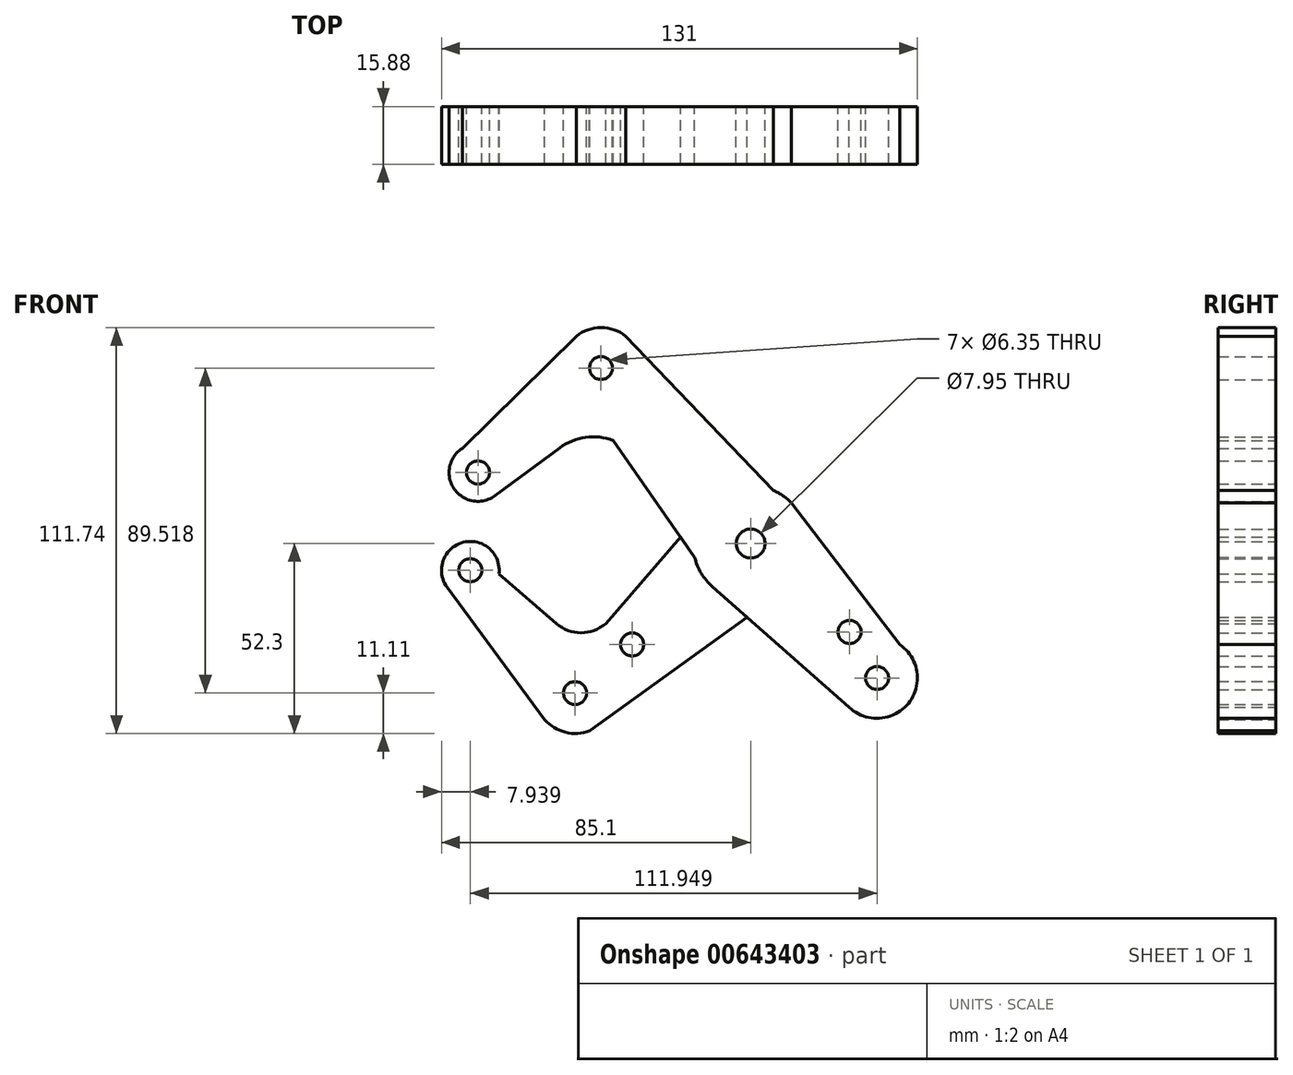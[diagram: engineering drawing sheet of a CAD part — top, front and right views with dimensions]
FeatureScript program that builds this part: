
annotation { "Feature Type Name" : "Feature", "Feature Type Description" : "" }
export const myFeature = defineFeature(function(context is Context, id is Id, definition is map)
    precondition{}
    {
        {
            var Q0;
            Q0=qCreatedBy(makeId("Front.planeOp"),FACE);
            var sketch = newSketch(context, id + "F0", { "sketchPlane" : qUnion([Q0])});
            skCircle(sketch, "E0", {"center": v(0, 0) * mm, "radius": 3.98 * mm});
            skCircle(sketch, "E1", {"center": v(0, 0) * mm, "radius": 15.88 * mm});
            skCircle(sketch, "E2", {"center": v(-41.19, 48.33) * mm, "radius": 11.11 * mm});
            skCircle(sketch, "E3", {"center": v(-41.19, 48.33) * mm, "radius": 3.18 * mm});
            skCircle(sketch, "E4", {"center": v(-75.06, 19.55) * mm, "radius": 3.18 * mm});
            skCircle(sketch, "E5", {"center": v(-75.06, 19.55) * mm, "radius": 7.94 * mm});
            skCircle(sketch, "E6", {"center": v(0, 0) * mm, "radius": 3.18 * mm});
            skCircle(sketch, "E7", {"center": v(34.79, -37.02) * mm, "radius": 3.18 * mm});
            skCircle(sketch, "E8", {"center": v(34.79, -37.02) * mm, "radius": 11.11 * mm});
            skLineSegment(sketch, "E9", {"start": v(-41.19, 48.33) * mm, "end": v(-75.06, 19.55) * mm, "construction": true});
            skLineSegment(sketch, "E10", {"start": v(-41.19, 48.33) * mm, "end": v(0, 0) * mm, "construction": true});
            skLineSegment(sketch, "E11", {"start": v(0, 0) * mm, "end": v(34.79, -37.02) * mm, "construction": true});
            skCircle(sketch, "E12", {"center": v(27.23, -24.34) * mm, "radius": 3.18 * mm});
            skLineSegment(sketch, "E13", {"start": v(0, 0) * mm, "end": v(-48.33, -41.19) * mm, "construction": true});
            skCircle(sketch, "E14", {"center": v(-48.33, -41.19) * mm, "radius": 11.11 * mm});
            skCircle(sketch, "E15", {"center": v(-48.33, -41.19) * mm, "radius": 3.18 * mm});
            skCircle(sketch, "E16", {"center": v(-32.61, -27.8) * mm, "radius": 3.18 * mm});
            skLineSegment(sketch, "E17", {"start": v(-48.33, -41.19) * mm, "end": v(-77.16, -7.36) * mm, "construction": true});
            skCircle(sketch, "E18", {"center": v(-77.16, -7.36) * mm, "radius": 3.18 * mm});
            skCircle(sketch, "E19", {"center": v(-77.16, -7.36) * mm, "radius": 7.94 * mm});
            skLineSegment(sketch, "E20", {"start": v(-79.35, 26.23) * mm, "end": v(-48.03, 57.09) * mm});
            skLineSegment(sketch, "E21", {"start": v(11.26, 11.2) * mm, "end": v(41.01, -27.81) * mm});
            skLineSegment(sketch, "E22", {"start": v(27.1, -45.04) * mm, "end": v(-12.2, -10.4) * mm});
            skLineSegment(sketch, "E23", {"start": v(-56.75, -48.44) * mm, "end": v(-83.55, -12.07) * mm});
            skLineSegment(sketch, "E24", {"start": v(-69.3, -8.4) * mm, "end": v(-53.49, -22.06) * mm});
            skArc(sketch, "E25", {"start": v(-53.49, -22.06) * mm, "mid": v(-46.7, -24.58) * mm, "end": v(-39.9, -22.06) * mm});
            skLineSegment(sketch, "E26", {"start": v(-39.9, -22.06) * mm, "end": v(-13.01, 9.1) * mm});
            skLineSegment(sketch, "E27", {"start": v(-44.26, -51.53) * mm, "end": v(10.96, -11.67) * mm});
            skLineSegment(sketch, "E28", {"start": v(-34.35, 57.09) * mm, "end": v(6.26, 14.59) * mm});
            skLineSegment(sketch, "E29", {"start": v(-70.34, 13.17) * mm, "end": v(-52.54, 26.34) * mm});
            skArc(sketch, "E30", {"start": v(-52.54, 26.34) * mm, "mid": v(-45.43, 29.24) * mm, "end": v(-37.8, 28.38) * mm});
            skLineSegment(sketch, "E31", {"start": v(-37.8, 28.38) * mm, "end": v(-15.43, -3.75) * mm});
            skSolve(sketch);
        }
        {
            var Q0;
            Q0=makeQuery(id+"F0.imprint","IMPRINT",FACE,{"disambiguationData":[TD([[makeQuery(id+"F0.imprint","IMPRINT",EDGE,{"derivedFrom":sQuery(id+"F0.wireOp",EDGE,"E16")}),-1.0]])]});
            var Q1;
            Q1=makeQuery(id+"F0.imprint","IMPRINT",FACE,{"disambiguationData":[TD([[makeQuery(id+"F0.imprint","IMPRINT",EDGE,{"derivedFrom":sQuery(id+"F0.wireOp",EDGE,"E18")}),-1.0]])]});
            var Q2;
            Q2=makeQuery(id+"F0.imprint","IMPRINT",FACE,{"disambiguationData":[TD([[makeQuery(id+"F0.imprint","IMPRINT",EDGE,{"derivedFrom":sQuery(id+"F0.wireOp",EDGE,"E15")}),-1.0]])]});
            extrude(context, id + "F1", {"entities" : qUnion([Q0, Q1, Q2]), "depth" : 15.88 * mm, "offsetDistance" : 25.4 * mm});
        }
        {
            var Q0;
            {var subQ0=sQuery(id+"F0.wireOp",EDGE,"E26");var subQ1=sQuery(id+"F0.wireOp",EDGE,"E1");var subQ2=makeQuery(id+"F0.imprint","INTERSECT",VERTEX,{"derivedFrom":[subQ1,subQ0]});Q0=makeQuery(id+"F0.imprint","IMPRINT",FACE,{"disambiguationData":[TD([[makeQuery(id+"F0.imprint","IMPRINT",EDGE,{"disambiguationData":[TD([[subQ2,-1.0]])],"derivedFrom":subQ1}),-1.0]])]});}
            var Q1;
            Q1=makeQuery(id+"F0.imprint","IMPRINT",FACE,{"disambiguationData":[TD([[makeQuery(id+"F0.imprint","IMPRINT",EDGE,{"derivedFrom":sQuery(id+"F0.wireOp",EDGE,"E0")}),-1.0]])]});
            var Q2;
            Q2=makeQuery(id+"F0.imprint","IMPRINT",FACE,{"disambiguationData":[TD([[makeQuery(id+"F0.imprint","IMPRINT",EDGE,{"derivedFrom":sQuery(id+"F0.wireOp",EDGE,"E12")}),-1.0]])]});
            var Q3;
            {var subQ0=sQuery(id+"F0.wireOp",EDGE,"E22");var subQ1=sQuery(id+"F0.wireOp",EDGE,"E1");var subQ2=makeQuery(id+"F0.imprint","INTERSECT",VERTEX,{"derivedFrom":[subQ1,subQ0]});Q3=makeQuery(id+"F0.imprint","IMPRINT",FACE,{"disambiguationData":[TD([[makeQuery(id+"F0.imprint","IMPRINT",EDGE,{"disambiguationData":[TD([[subQ2,-1.0]])],"derivedFrom":subQ1}),-1.0]])]});}
            var Q4;
            {var subQ10=sQuery(id+"F0.wireOp",EDGE,"E29");Q4=makeQuery(id+"F0.imprint","IMPRINT",FACE,{"disambiguationData":[TD([[makeQuery(id+"F0.imprint","IMPRINT",EDGE,{"derivedFrom":subQ10}),1.0]])]});}
            var Q5;
            Q5=makeQuery(id+"F0.imprint","IMPRINT",FACE,{"disambiguationData":[TD([[makeQuery(id+"F0.imprint","IMPRINT",EDGE,{"derivedFrom":sQuery(id+"F0.wireOp",EDGE,"E3")}),-1.0]])]});
            var Q6;
            Q6=makeQuery(id+"F0.imprint","IMPRINT",FACE,{"disambiguationData":[TD([[makeQuery(id+"F0.imprint","IMPRINT",EDGE,{"derivedFrom":sQuery(id+"F0.wireOp",EDGE,"E4")}),-1.0]])]});
            var Q7;
            Q7=makeQuery(id+"F0.imprint","IMPRINT",FACE,{"disambiguationData":[TD([[makeQuery(id+"F0.imprint","IMPRINT",EDGE,{"derivedFrom":sQuery(id+"F0.wireOp",EDGE,"E7")}),-1.0]])]});
            extrude(context, id + "F2", {"entities" : qUnion([Q0, Q1, Q2, Q3, Q4, Q5, Q6, Q7]), "depth" : 15.88 * mm, "offsetDistance" : 25.4 * mm});
        }
    });
